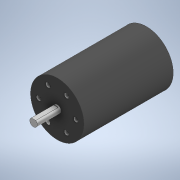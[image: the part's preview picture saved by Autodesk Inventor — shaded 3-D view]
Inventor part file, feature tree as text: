
AUTODESK INVENTOR PART (.ipt)
format: ipt  version: 2021 (Build 250183000, 183)  size: 126,464 bytes
history: native  units: mm
features: extrude x4, sketch x4
ambient origin geometry x8: Origin, YZ Plane, XZ Plane, XY Plane, X Axis, Y Axis, Z Axis, Center Point
bodies: Solid1 (feature_tree)
feature tree (8):
  extrude  "Extrusion1"  Depth=60.0mm TaperAngle=0.0deg
  extrude  "Extrusion2"  Depth=16.0mm TaperAngle=0.0deg
  extrude  "Extrusion3"  Depth=15.0mm TaperAngle=0.0deg
  extrude  "Extrusion4"  Depth=10.0mm
  sketch  "Sketch1"  dims[d0=36.0mm d1=60.0mm d2=0.0mm]
  sketch  "Sketch2"  dims[d3=5.0mm d4=16.0mm d5=0.0mm]
  sketch  "Sketch3"  dims[d6=4.5mm d7=15.0mm d8=0.0mm]
  sketch  "Sketch4"  dims[d9=3.0mm d10=12.5mm d11=60.0mm d13=360.0deg d15=10.0mm d16=0.0mm]
